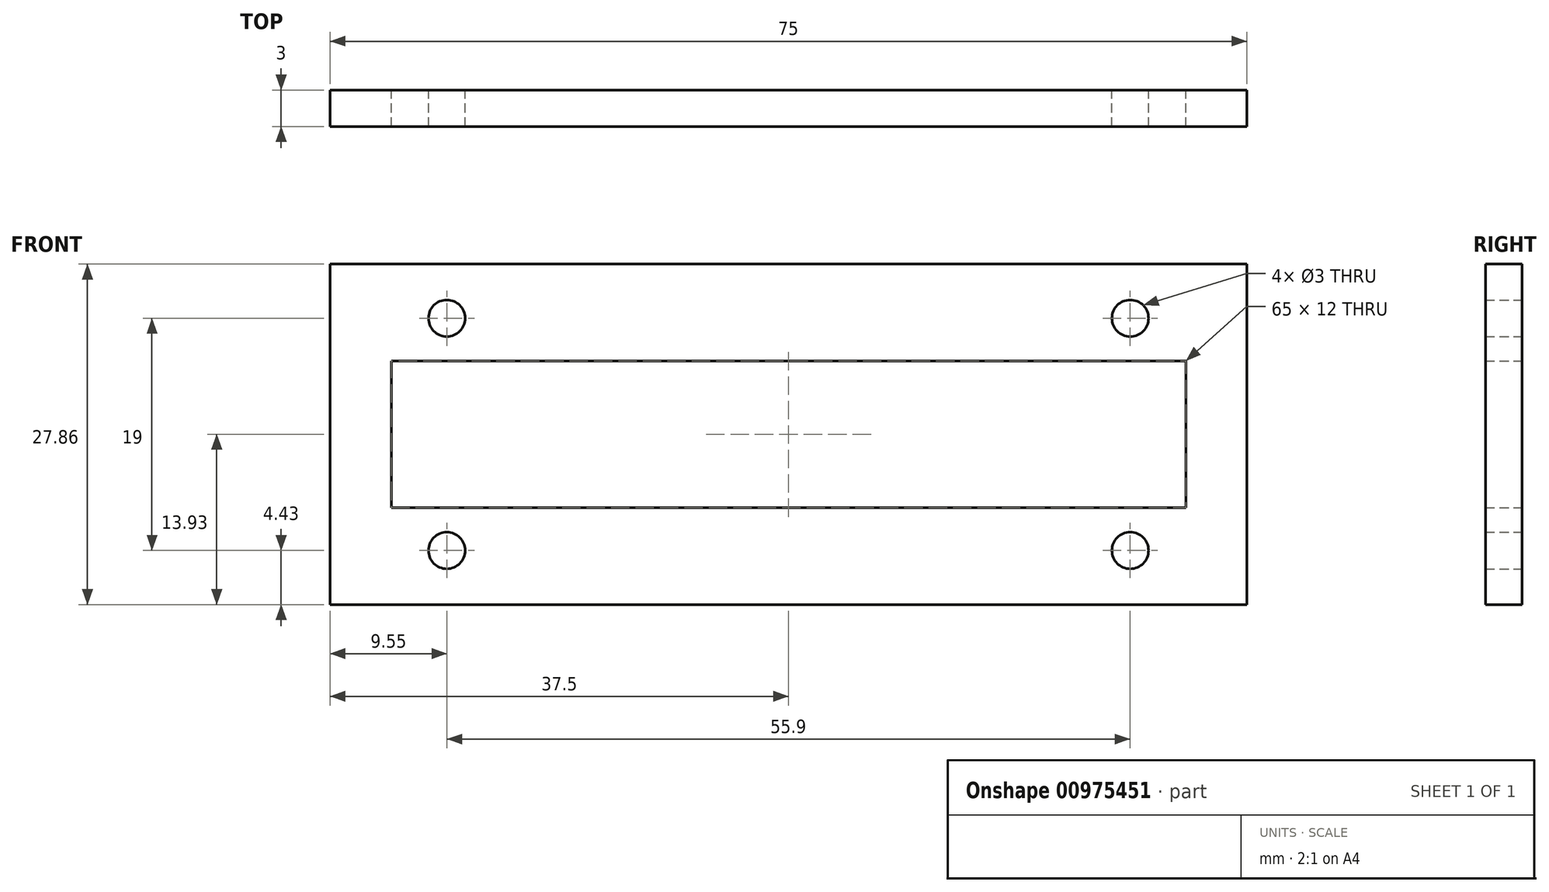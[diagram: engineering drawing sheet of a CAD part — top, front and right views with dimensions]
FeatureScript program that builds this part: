
annotation { "Feature Type Name" : "Feature", "Feature Type Description" : "" }
export const myFeature = defineFeature(function(context is Context, id is Id, definition is map)
    precondition{}
    {
        {
            var Q0;
            Q0=qCreatedBy(makeId("Front.planeOp"),FACE);
            var sketch = newSketch(context, id + "F0", { "sketchPlane" : qUnion([Q0])});
            skPoint(sketch, "E0.middle", {"position": v(0, 0) * mm});
            skCircle(sketch, "E1", {"center": v(-27.95, 9.5) * mm, "radius": 1.5 * mm});
            skCircle(sketch, "E2", {"center": v(27.95, 9.5) * mm, "radius": 1.5 * mm});
            skCircle(sketch, "E3", {"center": v(27.95, -9.5) * mm, "radius": 1.5 * mm});
            skCircle(sketch, "E4", {"center": v(-27.95, -9.5) * mm, "radius": 1.5 * mm});
            skLineSegment(sketch, "E5.bottom", {"start": v(37.5, 13.93) * mm, "end": v(-37.5, 13.93) * mm});
            skLineSegment(sketch, "E5.top", {"start": v(37.5, -13.93) * mm, "end": v(-37.5, -13.93) * mm});
            skLineSegment(sketch, "E5.left", {"start": v(37.5, 13.93) * mm, "end": v(37.5, -13.93) * mm});
            skLineSegment(sketch, "E5.right", {"start": v(-37.5, 13.93) * mm, "end": v(-37.5, -13.93) * mm});
            skLineSegment(sketch, "E6.bottom", {"start": v(32.5, 6) * mm, "end": v(-32.5, 6) * mm});
            skLineSegment(sketch, "E6.top", {"start": v(32.5, -6) * mm, "end": v(-32.5, -6) * mm});
            skLineSegment(sketch, "E6.left", {"start": v(32.5, 6) * mm, "end": v(32.5, -6) * mm});
            skLineSegment(sketch, "E6.right", {"start": v(-32.5, 6) * mm, "end": v(-32.5, -6) * mm});
            skSolve(sketch);
        }
        {
            var Q0;
            Q0=makeQuery(id+"F0.imprint","IMPRINT",FACE,{"disambiguationData":[TD([[makeQuery(id+"F0.imprint","IMPRINT",EDGE,{"derivedFrom":sQuery(id+"F0.wireOp",EDGE,"E1")}),-1.0]])]});
            extrude(context, id + "F1", {"entities" : qUnion([Q0]), "depth" : 3 * mm, "offsetDistance" : 25 * mm});
        }
    });
